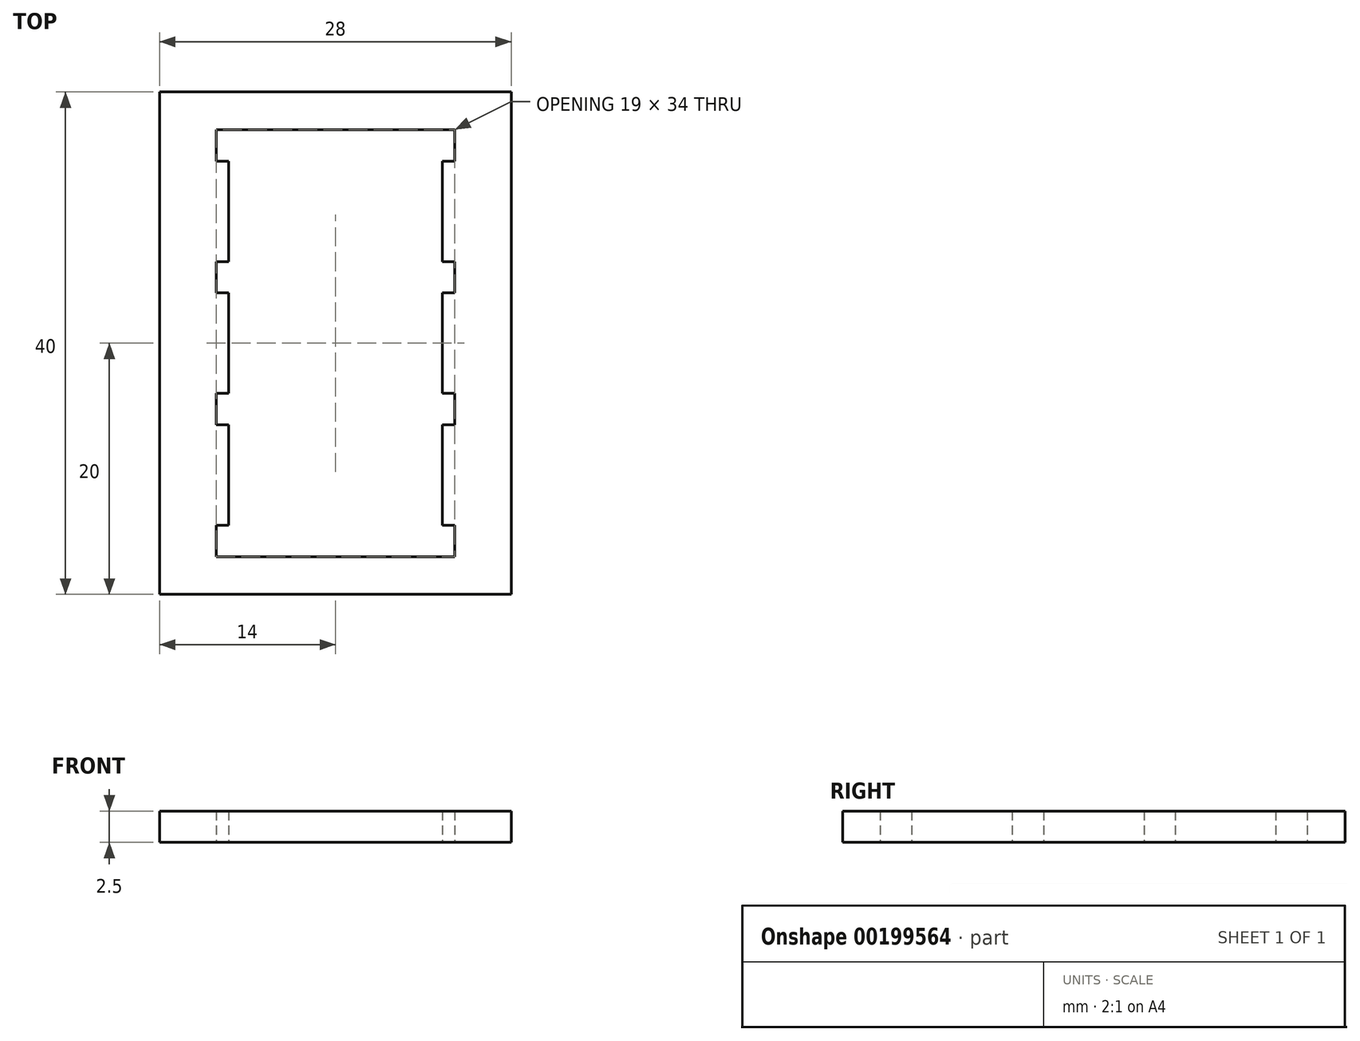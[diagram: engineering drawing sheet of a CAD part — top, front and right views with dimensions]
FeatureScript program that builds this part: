
annotation { "Feature Type Name" : "Feature", "Feature Type Description" : "" }
export const myFeature = defineFeature(function(context is Context, id is Id, definition is map)
    precondition{}
    {
        {
            var Q0;
            Q0=qCreatedBy(makeId("Top.planeOp"),FACE);
            var sketch = newSketch(context, id + "F0", { "sketchPlane" : qUnion([Q0])});
            skLineSegment(sketch, "E0.bottom", {"start": v(14, -20) * mm, "end": v(-14, -20) * mm});
            skLineSegment(sketch, "E0.top", {"start": v(14, 20) * mm, "end": v(-14, 20) * mm});
            skLineSegment(sketch, "E0.left", {"start": v(14, -20) * mm, "end": v(14, 20) * mm});
            skLineSegment(sketch, "E0.right", {"start": v(-14, -20) * mm, "end": v(-14, 20) * mm});
            skPoint(sketch, "E0.middle", {"position": v(0, 0) * mm});
            skLineSegment(sketch, "E1.bottom", {"start": v(9.5, -17) * mm, "end": v(-9.5, -17) * mm});
            skLineSegment(sketch, "E1.top", {"start": v(9.5, 17) * mm, "end": v(-9.5, 17) * mm});
            skLineSegment(sketch, "E1.left", {"start": v(9.5, -17) * mm, "end": v(9.5, -14.5) * mm});
            skLineSegment(sketch, "E1.right", {"start": v(-9.5, -17) * mm, "end": v(-9.5, -14.5) * mm});
            skLineSegment(sketch, "E2.left", {"start": v(8.5, -14.5) * mm, "end": v(8.5, -6.5) * mm});
            skLineSegment(sketch, "E2.right", {"start": v(-8.5, -14.5) * mm, "end": v(-8.5, -6.5) * mm});
            skLineSegment(sketch, "E3", {"start": v(-8.5, 14.5) * mm, "end": v(-9.5, 14.5) * mm});
            skLineSegment(sketch, "E4", {"start": v(8.5, 14.5) * mm, "end": v(9.5, 14.5) * mm});
            skLineSegment(sketch, "E5", {"start": v(-8.5, -14.5) * mm, "end": v(-9.5, -14.5) * mm});
            skLineSegment(sketch, "E6", {"start": v(8.5, -14.5) * mm, "end": v(9.5, -14.5) * mm});
            skLineSegment(sketch, "E7", {"start": v(-9.5, -4) * mm, "end": v(-8.5, -4) * mm});
            skLineSegment(sketch, "E8", {"start": v(-9.5, -6.5) * mm, "end": v(-8.5, -6.5) * mm});
            skLineSegment(sketch, "E9", {"start": v(-9.5, 4) * mm, "end": v(-8.5, 4) * mm});
            skLineSegment(sketch, "E10", {"start": v(-9.5, 6.5) * mm, "end": v(-8.5, 6.5) * mm});
            skLineSegment(sketch, "E11.trimOffspring", {"start": v(-9.5, 14.5) * mm, "end": v(-9.5, 17) * mm});
            skLineSegment(sketch, "E12.trimOffspring", {"start": v(-9.5, 4) * mm, "end": v(-9.5, 6.5) * mm});
            skLineSegment(sketch, "E13.trimOffspring", {"start": v(-9.5, -6.5) * mm, "end": v(-9.5, -4) * mm});
            skLineSegment(sketch, "E14.trimOffspring", {"start": v(9.5, 14.5) * mm, "end": v(9.5, 17) * mm});
            skLineSegment(sketch, "E15.trimOffspring", {"start": v(9.5, 4) * mm, "end": v(9.5, 6.5) * mm});
            skLineSegment(sketch, "E16.trimOffspring", {"start": v(9.5, -6.5) * mm, "end": v(9.5, -4) * mm});
            skLineSegment(sketch, "E17.trimOffspring", {"start": v(8.5, -4) * mm, "end": v(9.5, -4) * mm});
            skLineSegment(sketch, "E18.trimOffspring", {"start": v(8.5, -6.5) * mm, "end": v(9.5, -6.5) * mm});
            skLineSegment(sketch, "E19.trimOffspring", {"start": v(-8.5, -4) * mm, "end": v(-8.5, 4) * mm});
            skLineSegment(sketch, "E20.trimOffspring", {"start": v(8.5, -4) * mm, "end": v(8.5, 4) * mm});
            skLineSegment(sketch, "E21.trimOffspring", {"start": v(8.5, 6.5) * mm, "end": v(8.5, 14.5) * mm});
            skLineSegment(sketch, "E22.trimOffspring", {"start": v(8.5, 4) * mm, "end": v(9.5, 4) * mm});
            skLineSegment(sketch, "E23.trimOffspring", {"start": v(-8.5, 6.5) * mm, "end": v(-8.5, 14.5) * mm});
            skLineSegment(sketch, "E24.trimOffspring", {"start": v(8.5, 6.5) * mm, "end": v(9.5, 6.5) * mm});
            skSolve(sketch);
        }
        {
            var Q0;
            Q0=makeQuery(id+"F0.imprint","IMPRINT",FACE,{"disambiguationData":[TD([[makeQuery(id+"F0.imprint","IMPRINT",EDGE,{"derivedFrom":sQuery(id+"F0.wireOp",EDGE,"E0.bottom")}),-1.0]])]});
            extrude(context, id + "F1", {"entities" : qUnion([Q0]), "depth" : 2.5 * mm});
        }
    });
